# Revit family: SL421f616W - 1FP Family
name_source: partatom
category: Doors
revit_build: Autodesk Revit 2018 (Build: 20180329_1100(x64)
units: mm (PartAtom-declared; Revit-internal decimal feet)

## family parameters
Always vertical = Yes
Cut with Voids When Loaded = No
Host = Wall
OmniClass Number = 23.30.10.00
OmniClass Title = Doors
Room Calculation Point = No
Shared = No

## types (1)
- SL421F616W - 1FP
    Analytic Construction = Metal frame with single clear glass
    Distance = 36 mm  [stored 0.11811 ft]
    Door = White
    Door panel = 84 mm  [stored 0.275591 ft]
    Frame Projection Ext. = 25 mm  [stored 0.082021 ft]
    Frame Projection Int. = 25 mm  [stored 0.082021 ft]
    Frame Width = 75 mm  [stored 0.246063 ft]
    Function = Interior
    Glass = Glass
    Glass Thickness = 4 mm  [stored 0.0131234 ft]
    Heat Transfer Coefficient (U) = 6.5580 W/(m²·K)
    Height = 2090 mm  [stored 6.85696 ft]
    Manufacturer = Skyward Windows
    Model = SL421f616W - 1FP
    Solar Heat Gain Coefficient = 0
    Telephone = 021 276 1800
    Thermal Resistance (R) = 0.1525 (m²·K)/W
    URL = www.skywardwindows.co.za
    Visual Light Transmittance = 0
    Wall Closure = By host
    Width = 390 mm  [stored 1.27953 ft]

note: [stored X ft] marks values corroborated as IEEE doubles in the binary element streams (Revit-internal decimal feet)

## geometry (parser evidence)
native form markers: Blend x2, Sweep x3
no freeform markers — native parametric forms only
